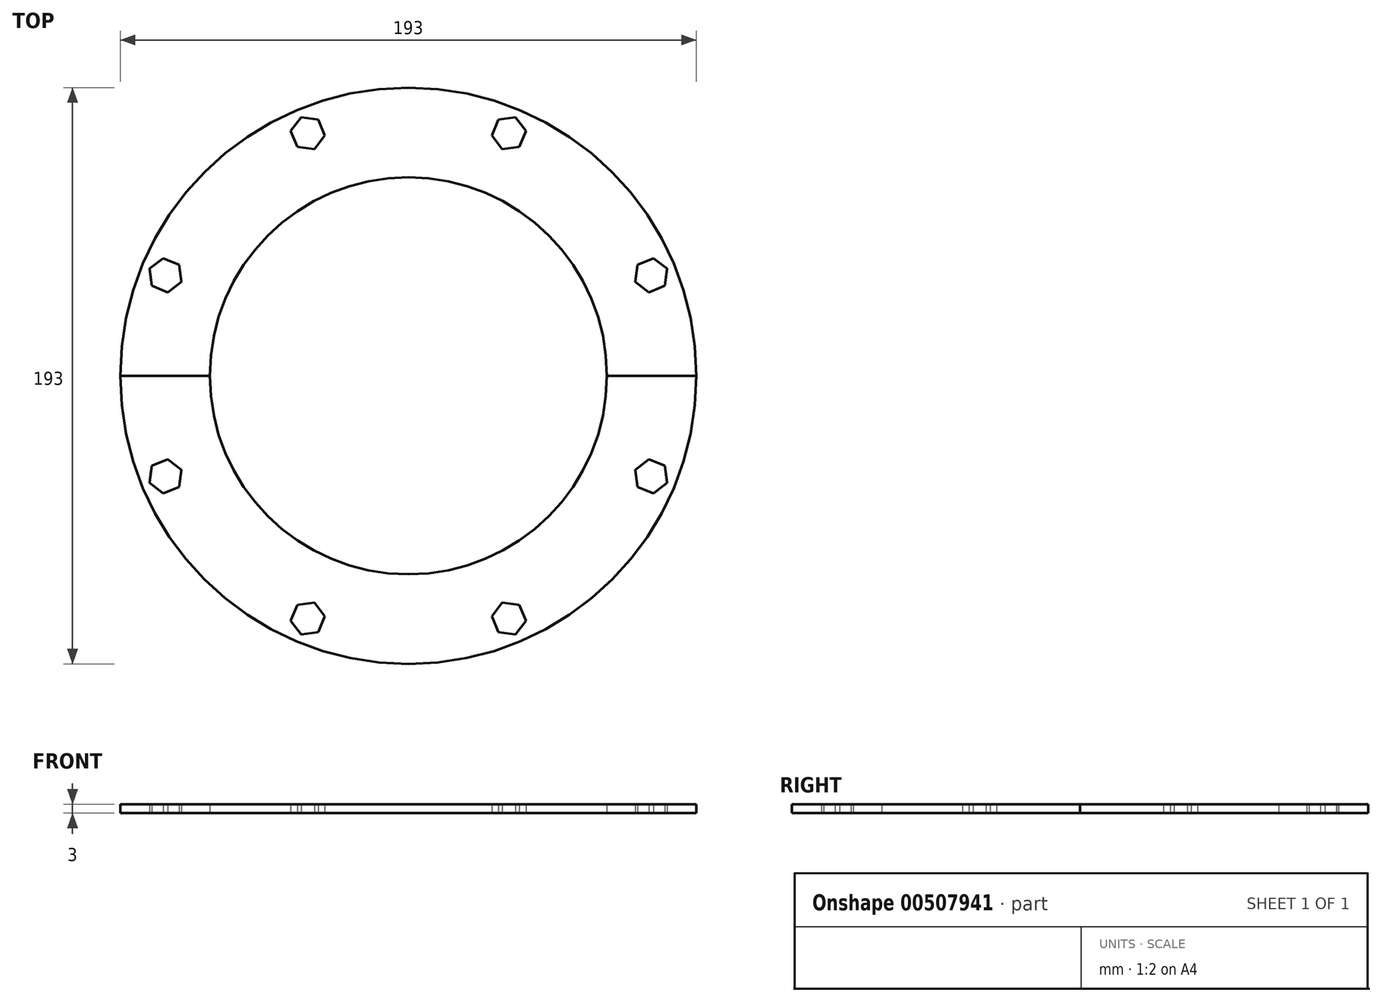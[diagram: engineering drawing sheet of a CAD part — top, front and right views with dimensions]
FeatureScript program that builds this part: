
annotation { "Feature Type Name" : "Feature", "Feature Type Description" : "" }
export const myFeature = defineFeature(function(context is Context, id is Id, definition is map)
    precondition{}
    {
        {
            var Q0;
            Q0=qCreatedBy(makeId("Top.planeOp"),FACE);
            var sketch = newSketch(context, id + "F0", { "sketchPlane" : qUnion([Q0])});
            skCircle(sketch, "E0", {"center": v(0, 0) * mm, "radius": 66.5 * mm, "construction": true});
            skCircle(sketch, "E1", {"center": v(0, 0) * mm, "radius": 96.5 * mm, "construction": true});
            skArc(sketch, "E2", {"start": v(-96.5, 0) * mm, "mid": v(0, 96.5) * mm, "end": v(96.5, 0) * mm});
            skArc(sketch, "E3", {"start": v(-66.5, 0) * mm, "mid": v(0, 66.5) * mm, "end": v(66.5, 0) * mm});
            skLineSegment(sketch, "E4", {"start": v(-66.5, 0) * mm, "end": v(-96.5, 0) * mm});
            skLineSegment(sketch, "E5", {"start": v(66.5, 0) * mm, "end": v(96.5, 0) * mm});
            skPoint(sketch, "E6", {"position": v(-81.5, 0) * mm});
            skCircle(sketch, "E7", {"center": v(0, 0) * mm, "radius": 81.5 * mm, "construction": true});
            skSolve(sketch);
        }
        {
            var Q0;
            Q0 = qSketchRegion(id + "F0", true);
            extrude(context, id + "F1", {"entities" : qUnion([Q0]), "depth" : 3 * mm, "offsetDistance" : 25 * mm});
        }
        {
            var Q0;
            Q0=qCreatedBy(makeId("Top.planeOp"),FACE);
            var sketch = newSketch(context, id + "F2", { "sketchPlane" : qUnion([Q0])});
            skCircle(sketch, "E8", {"center": v(0, 0) * mm, "radius": 88 * mm, "construction": true});
            skLineSegment(sketch, "E9.1.0", {"start": v(-82.06, 39.4) * mm, "end": v(-76.73, 37.2) * mm});
            skLineSegment(sketch, "E9.1.1", {"start": v(-75.96, 31.48) * mm, "end": v(-80.54, 27.95) * mm});
            skCircle(sketch, "E9.1.2", {"center": v(-81.3, 33.68) * mm, "radius": 5 * mm, "construction": true});
            skLineSegment(sketch, "E9.1.3", {"start": v(-85.88, 30.15) * mm, "end": v(-86.64, 35.88) * mm});
            skLineSegment(sketch, "E9.1.4", {"start": v(-76.73, 37.2) * mm, "end": v(-75.96, 31.48) * mm});
            skLineSegment(sketch, "E9.1.5", {"start": v(-80.54, 27.95) * mm, "end": v(-85.88, 30.15) * mm});
            skPoint(sketch, "E9.1.6", {"position": v(-84.35, 37.64) * mm});
            skLineSegment(sketch, "E9.1.7", {"start": v(-86.64, 35.88) * mm, "end": v(-82.06, 39.4) * mm});
            skLineSegment(sketch, "E9.anchor1", {"start": v(0, 0) * mm, "end": v(-88, 0) * mm, "construction": true});
            skLineSegment(sketch, "E9.anchor2", {"start": v(0, 0) * mm, "end": v(-81.3, 33.68) * mm, "construction": true});
            skLineSegment(sketch, "E10.1.0", {"start": v(-27.95, 80.56) * mm, "end": v(-31.46, 75.97) * mm});
            skLineSegment(sketch, "E10.1.1", {"start": v(-30.17, 85.89) * mm, "end": v(-27.95, 80.56) * mm});
            skLineSegment(sketch, "E10.1.2", {"start": v(-31.46, 75.97) * mm, "end": v(-37.18, 76.71) * mm});
            skLineSegment(sketch, "E10.1.3", {"start": v(-39.4, 82.05) * mm, "end": v(-35.9, 86.63) * mm});
            skLineSegment(sketch, "E10.1.4", {"start": v(-37.18, 76.71) * mm, "end": v(-39.4, 82.05) * mm});
            skCircle(sketch, "E10.1.5", {"center": v(-33.68, 81.3) * mm, "radius": 5 * mm, "construction": true});
            skLineSegment(sketch, "E10.1.6", {"start": v(-35.9, 86.63) * mm, "end": v(-30.17, 85.89) * mm});
            skPoint(sketch, "E10.1.7", {"position": v(-33.03, 86.26) * mm});
            skLineSegment(sketch, "E10.2.0", {"start": v(37.2, 76.73) * mm, "end": v(31.48, 75.96) * mm});
            skLineSegment(sketch, "E10.2.1", {"start": v(39.4, 82.06) * mm, "end": v(37.2, 76.73) * mm});
            skLineSegment(sketch, "E10.2.2", {"start": v(31.48, 75.96) * mm, "end": v(27.95, 80.54) * mm});
            skLineSegment(sketch, "E10.2.3", {"start": v(30.15, 85.88) * mm, "end": v(35.88, 86.64) * mm});
            skLineSegment(sketch, "E10.2.4", {"start": v(27.95, 80.54) * mm, "end": v(30.15, 85.88) * mm});
            skCircle(sketch, "E10.2.5", {"center": v(33.68, 81.3) * mm, "radius": 5 * mm, "construction": true});
            skLineSegment(sketch, "E10.2.6", {"start": v(35.88, 86.64) * mm, "end": v(39.4, 82.06) * mm});
            skPoint(sketch, "E10.2.7", {"position": v(37.64, 84.35) * mm});
            skLineSegment(sketch, "E10.anchor2", {"start": v(0, 0) * mm, "end": v(81.3, 33.68) * mm, "construction": true});
            skLineSegment(sketch, "E11.3.3.0", {"start": v(85.89, 30.17) * mm, "end": v(80.56, 27.95) * mm});
            skLineSegment(sketch, "E11.6.3.0", {"start": v(75.97, 31.46) * mm, "end": v(76.71, 37.18) * mm});
            skLineSegment(sketch, "E11.9.3.0", {"start": v(82.05, 39.4) * mm, "end": v(86.63, 35.9) * mm});
            skLineSegment(sketch, "E11.12.3.0", {"start": v(76.71, 37.18) * mm, "end": v(82.05, 39.4) * mm});
            skCircle(sketch, "E11.15.3.0", {"center": v(81.3, 33.68) * mm, "radius": 5 * mm, "construction": true});
            skLineSegment(sketch, "E11.16.3.0", {"start": v(80.56, 27.95) * mm, "end": v(75.97, 31.46) * mm});
            skLineSegment(sketch, "E11.17.3.0", {"start": v(86.63, 35.9) * mm, "end": v(85.89, 30.17) * mm});
            skPoint(sketch, "E11.20.3.0", {"position": v(86.26, 33.03) * mm});
            skSolve(sketch);
        }
        {
            var Q0;
            Q0 = qSketchRegion(id + "F2", true);
            extrude(context, id + "F3", {"entities" : qUnion([Q0]), "operationType" : NewBodyOperationType.REMOVE, "depth" : 3 * mm, "offsetDistance" : 25 * mm});
        }
        {
            var Q0;
            Q0=qCreatedBy(makeId("Top.planeOp"),FACE);
            var sketch = newSketch(context, id + "F4", { "sketchPlane" : qUnion([Q0])});
            skCircle(sketch, "E12", {"center": v(0, 0) * mm, "radius": 71.5 * mm});
            skCircle(sketch, "E13.0", {"center": v(0, 0) * mm, "radius": 66.5 * mm});
            skSolve(sketch);
        }
        {
            var Q0;
            Q0=makeQuery(id+"F1.opExtrude","SWEPT_BODY",BODY,{"disambiguationData":[OSD([sQuery(id+"F0.wireOp",EDGE,"E2"),sQuery(id+"F0.wireOp",EDGE,"E3"),sQuery(id+"F0.wireOp",EDGE,"E4"),sQuery(id+"F0.wireOp",EDGE,"E5")])]});
            var Q1;
            Q1=qCreatedBy(makeId("Front.planeOp"),FACE);
            mirror(context, id + "F5", {"entities" : qUnion([Q0]), "mirrorPlane" : qUnion([Q1])});
        }
    });
